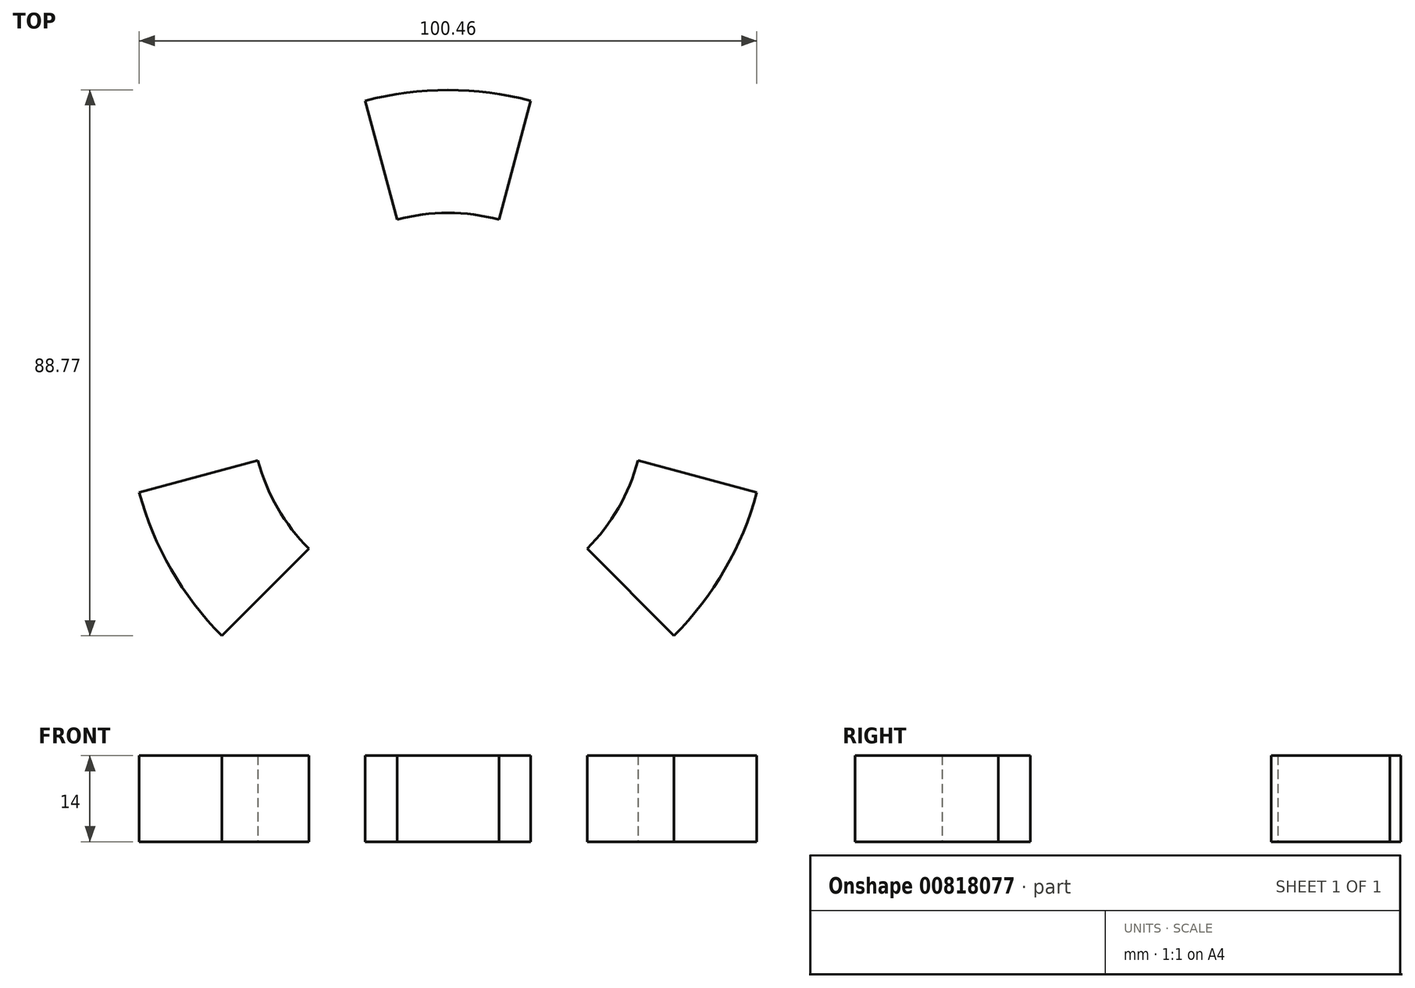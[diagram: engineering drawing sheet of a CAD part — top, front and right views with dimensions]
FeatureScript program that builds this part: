
annotation { "Feature Type Name" : "Feature", "Feature Type Description" : "" }
export const myFeature = defineFeature(function(context is Context, id is Id, definition is map)
    precondition{}
    {
        {
            var Q0;
            Q0=qCreatedBy(makeId("Top.planeOp"),FACE);
            var sketch = newSketch(context, id + "F0", { "sketchPlane" : qUnion([Q0])});
            skCircle(sketch, "E0", {"center": v(0, 0) * mm, "radius": 52 * mm});
            skCircle(sketch, "E1", {"center": v(0, 0) * mm, "radius": 28 * mm});
            skCircle(sketch, "E2", {"center": v(0, 0) * mm, "radius": 32 * mm});
            skLineSegment(sketch, "E3", {"start": v(0, 0) * mm, "end": v(0, 80.06) * mm});
            skLineSegment(sketch, "E4", {"start": v(0, -28) * mm, "end": v(0, -32) * mm});
            skLineSegment(sketch, "E5", {"start": v(0, 0) * mm, "end": v(-81.12, -46.83) * mm});
            skLineSegment(sketch, "E6", {"start": v(0, 0) * mm, "end": v(68.65, -39.63) * mm});
            skLineSegment(sketch, "E7", {"start": v(0, 0) * mm, "end": v(21.03, 78.5) * mm});
            skLineSegment(sketch, "E8", {"start": v(0, 0) * mm, "end": v(-20.05, 74.83) * mm});
            skLineSegment(sketch, "E9", {"start": v(0, 0) * mm, "end": v(-94.25, -25.26) * mm});
            skLineSegment(sketch, "E10", {"start": v(0, 0) * mm, "end": v(-57.02, -57.02) * mm});
            skLineSegment(sketch, "E11", {"start": v(0, 0) * mm, "end": v(53.16, -53.16) * mm});
            skLineSegment(sketch, "E12", {"start": v(0, 0) * mm, "end": v(77.92, -20.88) * mm});
            skSolve(sketch);
        }
        {
            var Q0;
            {var subQ0=sQuery(id+"F0.wireOp",EDGE,"E3");var subQ1=sQuery(id+"F0.wireOp",EDGE,"E0");var subQ2=makeQuery(id+"F0.imprint","INTERSECT",VERTEX,{"derivedFrom":[subQ1,subQ0]});Q0=makeQuery(id+"F0.imprint","IMPRINT",FACE,{"disambiguationData":[TD([[makeQuery(id+"F0.imprint","IMPRINT",EDGE,{"disambiguationData":[TD([[subQ2,1.0]])],"derivedFrom":subQ1}),1.0]])]});}
            var Q1;
            {var subQ0=sQuery(id+"F0.wireOp",EDGE,"E3");var subQ1=sQuery(id+"F0.wireOp",EDGE,"E0");var subQ2=makeQuery(id+"F0.imprint","INTERSECT",VERTEX,{"derivedFrom":[subQ1,subQ0]});Q1=makeQuery(id+"F0.imprint","IMPRINT",FACE,{"disambiguationData":[TD([[makeQuery(id+"F0.imprint","IMPRINT",EDGE,{"disambiguationData":[TD([[subQ2,-1.0]])],"derivedFrom":subQ1}),1.0]])]});}
            extrude(context, id + "F1", {"entities" : qUnion([Q0, Q1]), "depth" : 14 * mm, "offsetDistance" : 25 * mm});
        }
        {
            var Q0;
            {var subQ0=sQuery(id+"F0.wireOp",EDGE,"E9");var subQ1=sQuery(id+"F0.wireOp",EDGE,"E0");var subQ2=makeQuery(id+"F0.imprint","INTERSECT",VERTEX,{"derivedFrom":[subQ1,subQ0]});Q0=makeQuery(id+"F0.imprint","IMPRINT",FACE,{"disambiguationData":[TD([[makeQuery(id+"F0.imprint","IMPRINT",EDGE,{"disambiguationData":[TD([[subQ2,-1.0]])],"derivedFrom":subQ1}),1.0]])]});}
            var Q1;
            {var subQ0=sQuery(id+"F0.wireOp",EDGE,"E5");var subQ1=sQuery(id+"F0.wireOp",EDGE,"E0");var subQ2=makeQuery(id+"F0.imprint","INTERSECT",VERTEX,{"derivedFrom":[subQ1,subQ0]});Q1=makeQuery(id+"F0.imprint","IMPRINT",FACE,{"disambiguationData":[TD([[makeQuery(id+"F0.imprint","IMPRINT",EDGE,{"disambiguationData":[TD([[subQ2,-1.0]])],"derivedFrom":subQ1}),1.0]])]});}
            var Q2;
            {var subQ0=sQuery(id+"F0.wireOp",EDGE,"E3");var subQ1=sQuery(id+"F0.wireOp",EDGE,"E0");var subQ2=makeQuery(id+"F0.imprint","INTERSECT",VERTEX,{"derivedFrom":[subQ1,subQ0]});Q2=makeQuery(id+"F0.imprint","IMPRINT",FACE,{"disambiguationData":[TD([[makeQuery(id+"F0.imprint","IMPRINT",EDGE,{"disambiguationData":[TD([[subQ2,-1.0]])],"derivedFrom":subQ1}),1.0]])]});}
            var Q3;
            {var subQ0=sQuery(id+"F0.wireOp",EDGE,"E3");var subQ1=sQuery(id+"F0.wireOp",EDGE,"E0");var subQ2=makeQuery(id+"F0.imprint","INTERSECT",VERTEX,{"derivedFrom":[subQ1,subQ0]});Q3=makeQuery(id+"F0.imprint","IMPRINT",FACE,{"disambiguationData":[TD([[makeQuery(id+"F0.imprint","IMPRINT",EDGE,{"disambiguationData":[TD([[subQ2,1.0]])],"derivedFrom":subQ1}),1.0]])]});}
            var Q4;
            {var subQ0=sQuery(id+"F0.wireOp",EDGE,"E6");var subQ1=sQuery(id+"F0.wireOp",EDGE,"E0");var subQ2=makeQuery(id+"F0.imprint","INTERSECT",VERTEX,{"derivedFrom":[subQ1,subQ0]});Q4=makeQuery(id+"F0.imprint","IMPRINT",FACE,{"disambiguationData":[TD([[makeQuery(id+"F0.imprint","IMPRINT",EDGE,{"disambiguationData":[TD([[subQ2,-1.0]])],"derivedFrom":subQ1}),1.0]])]});}
            var Q5;
            {var subQ0=sQuery(id+"F0.wireOp",EDGE,"E11");var subQ1=sQuery(id+"F0.wireOp",EDGE,"E0");var subQ2=makeQuery(id+"F0.imprint","INTERSECT",VERTEX,{"derivedFrom":[subQ1,subQ0]});Q5=makeQuery(id+"F0.imprint","IMPRINT",FACE,{"disambiguationData":[TD([[makeQuery(id+"F0.imprint","IMPRINT",EDGE,{"disambiguationData":[TD([[subQ2,-1.0]])],"derivedFrom":subQ1}),1.0]])]});}
            extrude(context, id + "F2", {"entities" : qUnion([Q0, Q1, Q2, Q3, Q4, Q5]), "operationType" : NewBodyOperationType.ADD, "depth" : 14 * mm, "offsetDistance" : 25 * mm});
        }
    });
